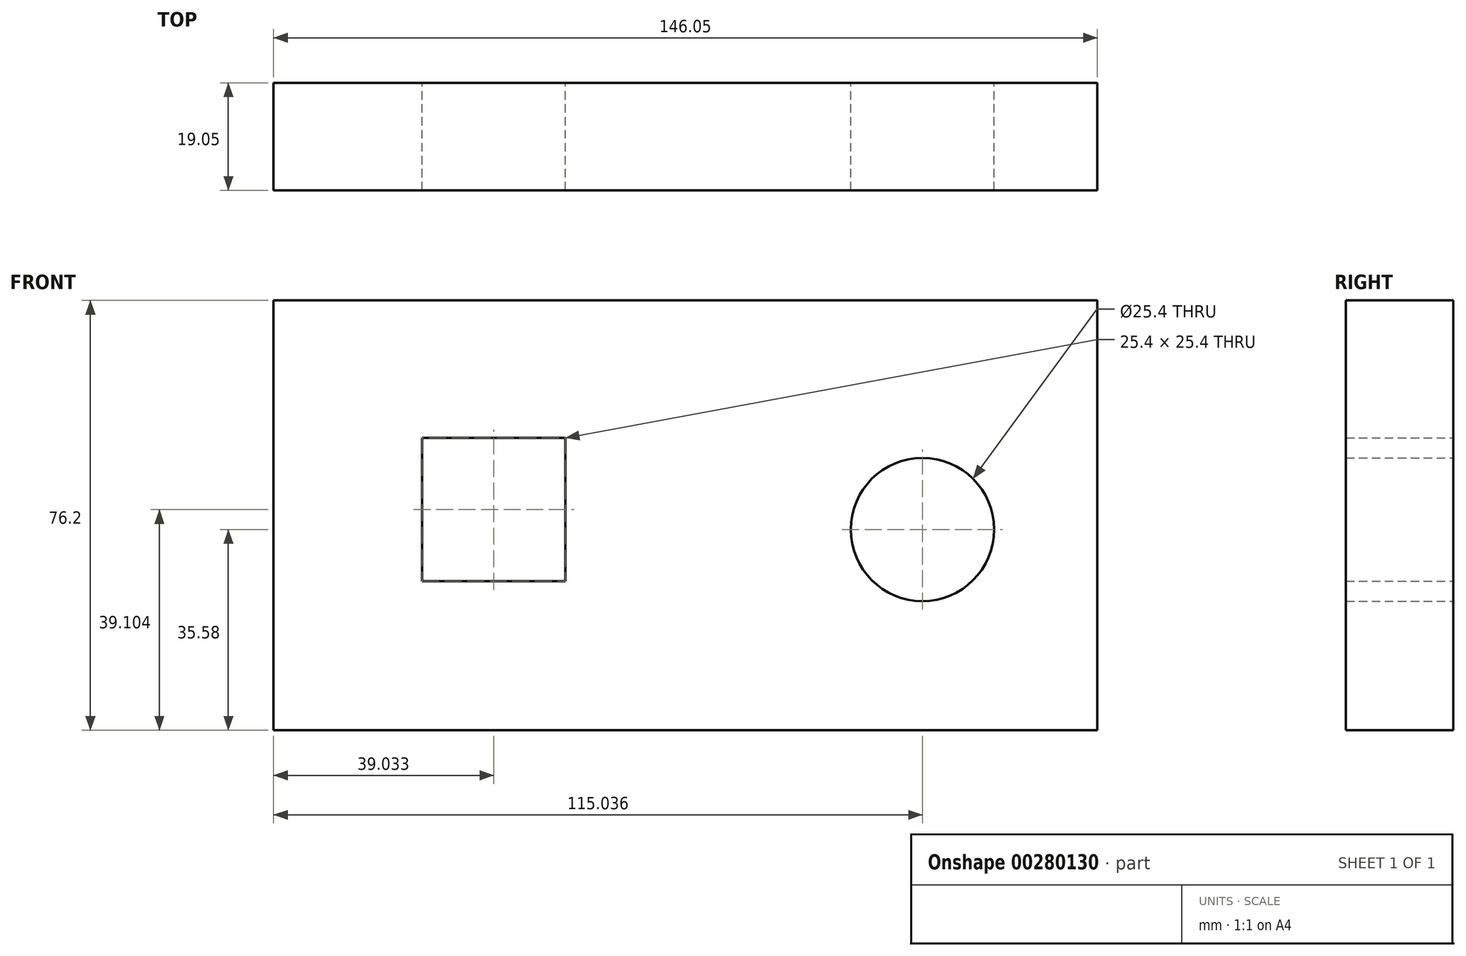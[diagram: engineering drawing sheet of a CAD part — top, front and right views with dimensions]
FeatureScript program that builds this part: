
annotation { "Feature Type Name" : "Feature", "Feature Type Description" : "" }
export const myFeature = defineFeature(function(context is Context, id is Id, definition is map)
    precondition{}
    {
        {
            var Q0;
            Q0=qCreatedBy(makeId("Front.planeOp"),FACE);
            var sketch = newSketch(context, id + "F0", { "sketchPlane" : qUnion([Q0])});
            skLineSegment(sketch, "E0.bottom", {"start": v(0, 0) * mm, "end": v(-146.05, 0) * mm});
            skLineSegment(sketch, "E0.top", {"start": v(0, 76.2) * mm, "end": v(-146.05, 76.2) * mm});
            skLineSegment(sketch, "E0.left", {"start": v(0, 0) * mm, "end": v(0, 76.2) * mm});
            skLineSegment(sketch, "E0.right", {"start": v(-146.05, 0) * mm, "end": v(-146.05, 76.2) * mm});
            skCircle(sketch, "E1", {"center": v(-31.01, 35.58) * mm, "radius": 12.7 * mm});
            skLineSegment(sketch, "E2.bottom", {"start": v(-119.72, 26.4) * mm, "end": v(-94.32, 26.4) * mm});
            skLineSegment(sketch, "E2.top", {"start": v(-119.72, 51.8) * mm, "end": v(-94.32, 51.8) * mm});
            skLineSegment(sketch, "E2.left", {"start": v(-119.72, 26.4) * mm, "end": v(-119.72, 51.8) * mm});
            skLineSegment(sketch, "E2.right", {"start": v(-94.32, 26.4) * mm, "end": v(-94.32, 51.8) * mm});
            skSolve(sketch);
        }
        {
            var Q0;
            Q0 = qSketchRegion(id + "F0", true);
            extrude(context, id + "F1", {"entities" : qUnion([Q0]), "depth" : 19.05 * mm});
        }
    });
